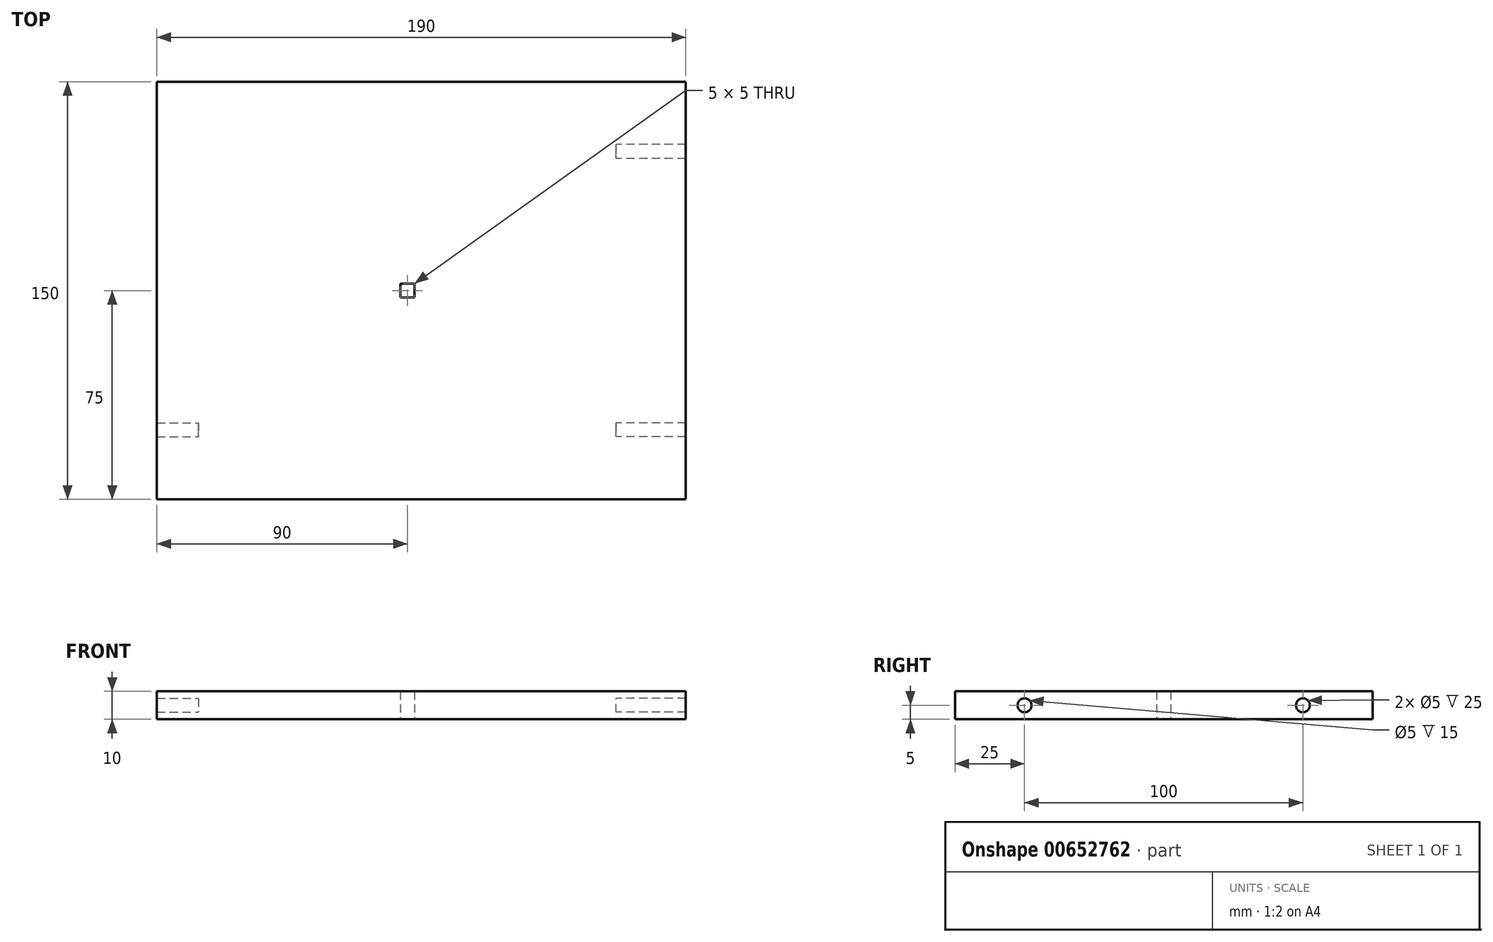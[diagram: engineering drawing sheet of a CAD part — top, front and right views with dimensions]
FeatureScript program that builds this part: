
annotation { "Feature Type Name" : "Feature", "Feature Type Description" : "" }
export const myFeature = defineFeature(function(context is Context, id is Id, definition is map)
    precondition{}
    {
        {
            var Q0;
            Q0=qCreatedBy(makeId("Top.planeOp"),FACE);
            var sketch = newSketch(context, id + "F0", { "sketchPlane" : qUnion([Q0])});
            skLineSegment(sketch, "E0.bottom", {"start": v(-75, 75) * mm, "end": v(75, 75) * mm});
            skLineSegment(sketch, "E0.top", {"start": v(-75, -75) * mm, "end": v(75, -75) * mm});
            skLineSegment(sketch, "E0.left", {"start": v(-75, 75) * mm, "end": v(-75, -75) * mm});
            skLineSegment(sketch, "E0.right", {"start": v(75, 75) * mm, "end": v(75, -75) * mm});
            skPoint(sketch, "E0.middle", {"position": v(0, 0) * mm});
            skLineSegment(sketch, "E1.bottom", {"start": v(-2.5, 2.5) * mm, "end": v(2.5, 2.5) * mm});
            skLineSegment(sketch, "E1.top", {"start": v(-2.5, -2.5) * mm, "end": v(2.5, -2.5) * mm});
            skLineSegment(sketch, "E1.left", {"start": v(-2.5, 2.5) * mm, "end": v(-2.5, -2.5) * mm});
            skLineSegment(sketch, "E1.right", {"start": v(2.5, 2.5) * mm, "end": v(2.5, -2.5) * mm});
            skSolve(sketch);
        }
        {
            var Q0;
            Q0=makeQuery(id+"F0.imprint","IMPRINT",FACE,{"disambiguationData":[TD([[makeQuery(id+"F0.imprint","IMPRINT",EDGE,{"derivedFrom":sQuery(id+"F0.wireOp",EDGE,"E0.bottom")}),-1.0]])]});
            extrude(context, id + "F1", {"entities" : qUnion([Q0]), "depth" : 10 * mm, "offsetDistance" : 25 * mm});
        }
        {
            var Q0;
            Q0=makeQuery(id+"F1.opExtrude","SWEPT_FACE",FACE,{"disambiguationData":[OSD([sQuery(id+"F0.wireOp",EDGE,"E0.right")])]});
            var sketch = newSketch(context, id + "F2", { "sketchPlane" : qUnion([Q0])});
            skLineSegment(sketch, "E2", {"start": v(0, 0) * mm, "end": v(0, 20.02) * mm, "construction": true});
            skLineSegment(sketch, "E3", {"start": v(0, 0) * mm, "end": v(0, -17.56) * mm});
            skCircle(sketch, "E4", {"center": v(-50, 5) * mm, "radius": 2.5 * mm});
            skCircle(sketch, "E5", {"center": v(50, 5) * mm, "radius": 2.5 * mm});
            skSolve(sketch);
        }
        {
            var Q0;
            Q0=makeQuery(id+"F2.imprint","IMPRINT",FACE,{"disambiguationData":[TD([[makeQuery(id+"F2.imprint","IMPRINT",EDGE,{"derivedFrom":sQuery(id+"F2.wireOp",EDGE,"E4")}),-1.0]])]});
            var sketch = newSketch(context, id + "F3", { "sketchPlane" : qUnion([Q0])});
            skSolve(sketch);
        }
        {
            var Q0;
            Q0 = qSketchRegion(id + "F3", true);
            var Q1;
            Q1=makeQuery(id+"F3.imprint","IMPRINT",FACE,{"disambiguationData":[TD([[makeQuery(id+"F3.imprint","IMPRINT",EDGE,{"derivedFrom":makeQuery(id+"F2.imprint","IMPRINT",EDGE,{"derivedFrom":sQuery(id+"F2.wireOp",EDGE,"E4")})}),-1.0]])]});
            extrude(context, id + "F4", {"entities" : qUnion([Q0, Q1]), "operationType" : NewBodyOperationType.ADD, "depth" : 25 * mm, "offsetDistance" : 25 * mm});
        }
        {
            var Q0;
            Q0=makeQuery(id+"F1.opExtrude","SWEPT_FACE",FACE,{"disambiguationData":[OSD([sQuery(id+"F0.wireOp",EDGE,"E0.left")])]});
            var sketch = newSketch(context, id + "F5", { "sketchPlane" : qUnion([Q0])});
            skCircle(sketch, "E6", {"center": v(50, 5) * mm, "radius": 2.5 * mm});
            skCircle(sketch, "E7", {"center": v(-50, 5) * mm, "radius": 2.5 * mm});
            skSolve(sketch);
        }
        {
            var Q0;
            Q0=makeQuery(id+"F5.imprint","IMPRINT",FACE,{"disambiguationData":[TD([[makeQuery(id+"F5.imprint","IMPRINT",EDGE,{"derivedFrom":sQuery(id+"F5.wireOp",EDGE,"E6")}),-1.0]])]});
            extrude(context, id + "F6", {"entities" : qUnion([Q0]), "operationType" : NewBodyOperationType.ADD, "depth" : 15 * mm, "offsetDistance" : 25 * mm});
        }
        {
            var Q0;
            Q0=makeQuery(id+"F5.imprint","IMPRINT",FACE,{"disambiguationData":[TD([[makeQuery(id+"F5.imprint","IMPRINT",EDGE,{"derivedFrom":sQuery(id+"F5.wireOp",EDGE,"E7")}),1.0]])]});
            extrude(context, id + "F7", {"entities" : qUnion([Q0]), "operationType" : NewBodyOperationType.ADD, "depth" : 15 * mm, "offsetDistance" : 25 * mm});
        }
    });
